# Revit family: NBS_DudleyIndustries_HndDriers_BehindTheMirrorRange_WarmAirDryer
name_source: partatom
category: Specialty Equipment
revit_build: Autodesk Revit 2016 (Build: 20150220_1215(x64)
units: mm (PartAtom-declared; Revit-internal decimal feet)

## family parameters
Cut with Voids When Loaded = No
Host = Face
OmniClass Number = 23.40.20.21.14
OmniClass Title = Hand and Hair Dryers
Part Type = Normal
Room Calculation Point = No
Round Connector Dimension = Use Diameter
Shared = No

## types (1)
- BehindTheMirrorRangeWarmAirDryer
    AssetType = Fixed
    BIMObjectName = NBS_DudleyIndustries_HandDriers_BehindTheMirrorRange_WarmAirDryer
    BodyEnclosure = Stainless Steel
    BodyFinishColour = Brushed
    BodyIngressProtectionMinimum = IP21
    Category = Pr_40_70_62_37:Hand driers
    CodePerformance = CE, BS EN 60335-2-23:2003 + A1:2008 (Particular Requirements for Appliances for skin and hair Care) and BS EN 60335-1:2002 + A2:2006 (incorporating A1,A11,A12, A13)(Safety of Household and similar electrical appliances), EN 55014-1: 2006 + A1: 2009, EN 55014-2: 1997 + A1: 2001 + A2:2008, EN 61000-3-2: 2006, EN 61000-3-3: 2008, RoHS, WEEE
    Color = Stainless steel
    Default Elevation = 1200 mm
    Description = Discreetly hidden within the ‘behind the mirror’ cavity Warm Air Dryer
    DryerMaterial = NBS_Concept
    DurationUnit = year
    ElectricalDeviceNominalPower = 1.7
    ElectricalSupplyPowerRating = 1.7kW @230 volts
    ElectricalSupplyRatedOperationalVoltageUe = 230 V ac
    ExpectedLife = 3
    Features = Discreetly hidden within the ‘behind the mirror’ cavity Warm Air Dryer, automatic start/stop, CE approved, suitable for high traffic locations
    Finish = Brushed
    Form = High performance warm air hand dryer
    Grade = EN1.4509
    HasProtectiveEarth = Yes
    IP_Code = IP21
    IfcExportAs = IfcElectricApplianceType
    IfcExportType = HANDDRYER
    ManufacturerName = Dudley Industries
    ManufacturerURL = www.dudleyindustries.com/
    Material = Stainless steel
    ModelNumber = 92022SS
    ModelReference = Behind the Mirror Range: Warm Air Dryer
    NBSCertification = www.nationalbimlibrary.com/cert/nj3q1dtx
    NBSDescription = Hand driers
    NBSReference = 45-35-72/334
    Name = HandDriers_BehindTheMirrorRange_WarmAirDryer_DudleyIndustries
    NoiseLevel = 71 dBA
    NominalCurrent = 0
    NominalFrequencyRange = 50 - 60 Hz
    NominalHeight = 346 mm  [stored 1.13517 ft]
    NominalLength = 100 mm  [stored 0.328084 ft]
    NominalVoltage = 0
    NominalWidth = 306 mm  [stored 1.00394 ft]
    NumberOfPoles = 0
    Operation = Automatic start/stop
    PhaseAngle = 0.00°
    ProductInformation = www.dudleyindustries.com/wp-content/uploads/2016/11/Warm-Air-Dryer.pdf
    Size = 306 x 346 x 100 mm
    Uniclass2015Code = Pr_40_70_62_37
    Uniclass2015Title = Hand driers
    Uniclass2015Version = Products v1.7
    UsageCurrent = 7.8
    Version = 2
    WarrantyDescription = 1 year warranty
    WarrantyDurationParts = 1
    WarrantyDurationUnit = year

note: [stored X ft] marks values corroborated as IEEE doubles in the binary element streams (Revit-internal decimal feet)

## geometry (parser evidence)
native form markers: Sweep x2
no freeform markers — native parametric forms only
